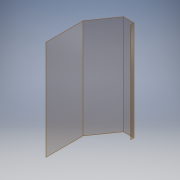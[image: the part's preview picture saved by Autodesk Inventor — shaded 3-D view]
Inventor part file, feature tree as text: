
AUTODESK INVENTOR PART (.ipt)
format: ipt  version: 2018 (Build 220112000, 112)  size: 108,544 bytes
history: native  units: mm
features: extrude x1, sketch x1
ambient origin geometry x8: Origin, YZ Plane, XZ Plane, XY Plane, X Axis, Y Axis, Z Axis, Center Point
bodies: Solid1 (feature_tree)
feature tree (2):
  extrude  "Extrusion1"  Depth=130.0mm
  sketch  "Sketch1"  dims[d0=40.0mm d1=130.0mm d2=21.816616mm d3=350.0mm d4=448.421mm d5=4.0mm d6=1200.0mm d7=0.0mm]
